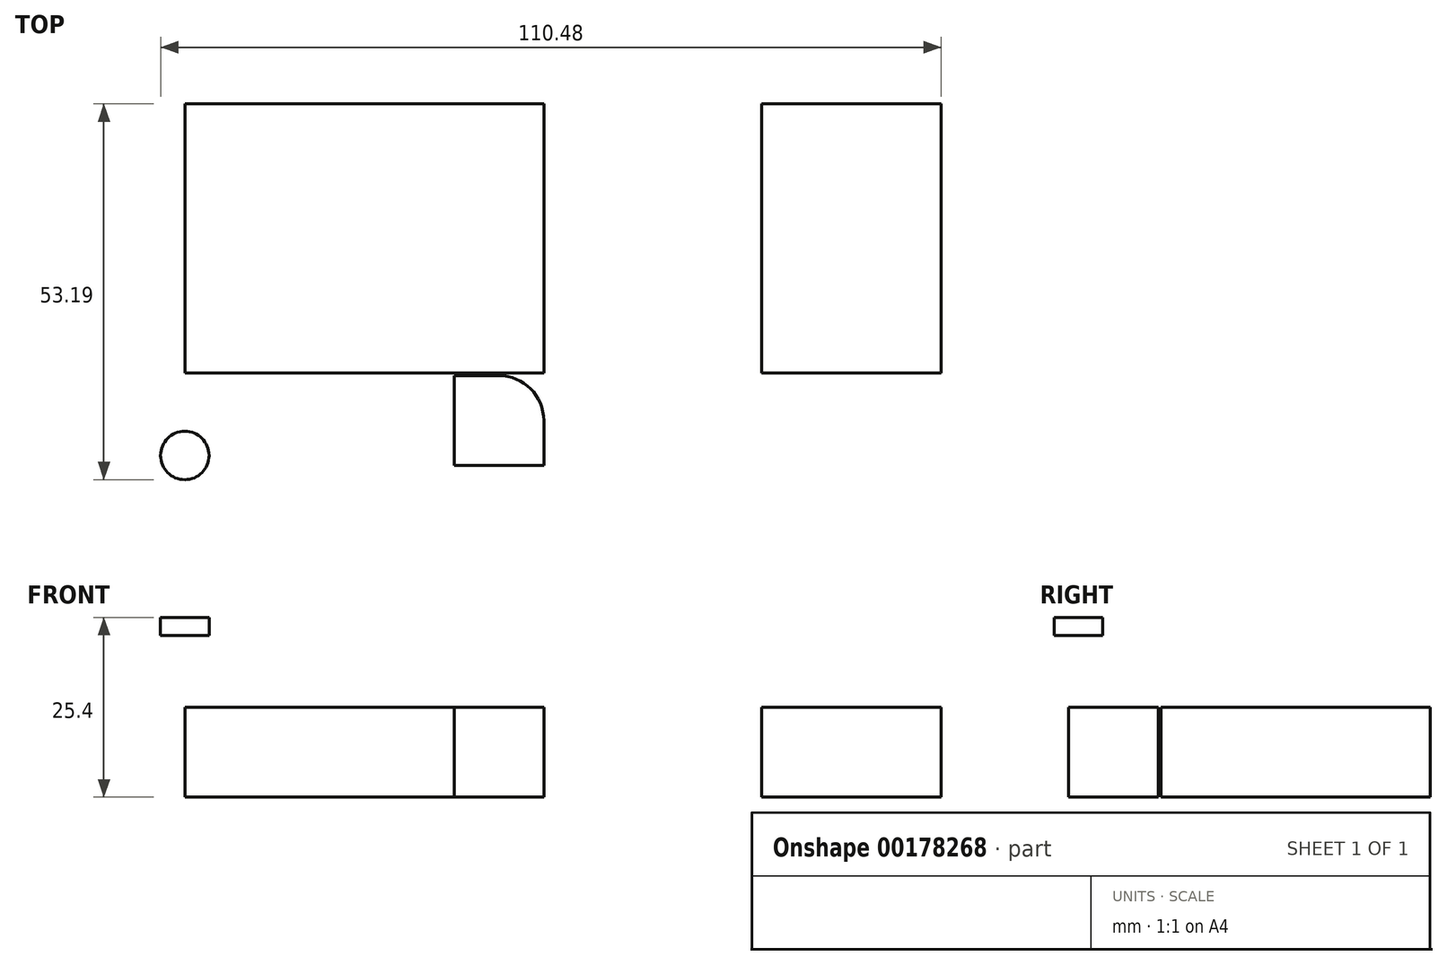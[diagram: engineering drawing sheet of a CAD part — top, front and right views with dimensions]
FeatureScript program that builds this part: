
annotation { "Feature Type Name" : "Feature", "Feature Type Description" : "" }
export const myFeature = defineFeature(function(context is Context, id is Id, definition is map)
    precondition{}
    {
        {
            var Q0;
            Q0=qCreatedBy(makeId("Top.planeOp"),FACE);
            var sketch = newSketch(context, id + "F0", { "sketchPlane" : qUnion([Q0])});
            skLineSegment(sketch, "E0.bottom", {"start": v(0, 0) * mm, "end": v(107.05, 0) * mm});
            skLineSegment(sketch, "E0.top", {"start": v(0, 66.76) * mm, "end": v(107.05, 66.76) * mm});
            skLineSegment(sketch, "E0.left", {"start": v(0, 0) * mm, "end": v(0, 66.76) * mm});
            skLineSegment(sketch, "E0.right", {"start": v(107.05, 0) * mm, "end": v(107.05, 66.76) * mm});
            skSolve(sketch);
        }
        {
            var Q0;
            Q0=qCreatedBy(makeId("Top.planeOp"),FACE);
            var sketch = newSketch(context, id + "F1", { "sketchPlane" : qUnion([Q0])});
            skLineSegment(sketch, "E1.bottom", {"start": v(0, 28.66) * mm, "end": v(50.8, 28.66) * mm});
            skLineSegment(sketch, "E1.top", {"start": v(0, 66.76) * mm, "end": v(50.8, 66.76) * mm});
            skLineSegment(sketch, "E1.left", {"start": v(0, 28.66) * mm, "end": v(0, 66.76) * mm});
            skLineSegment(sketch, "E1.right", {"start": v(50.8, 28.66) * mm, "end": v(50.8, 66.76) * mm});
            skLineSegment(sketch, "E2.bottom", {"start": v(81.65, 66.76) * mm, "end": v(107.05, 66.76) * mm});
            skLineSegment(sketch, "E2.top", {"start": v(81.65, 28.66) * mm, "end": v(107.05, 28.66) * mm});
            skLineSegment(sketch, "E2.left", {"start": v(81.65, 66.76) * mm, "end": v(81.65, 28.66) * mm});
            skLineSegment(sketch, "E2.right", {"start": v(107.05, 66.76) * mm, "end": v(107.05, 28.66) * mm});
            skLineSegment(sketch, "E3.bottom", {"start": v(38.1, 28.3) * mm, "end": v(44.45, 28.3) * mm});
            skLineSegment(sketch, "E3.top", {"start": v(38.1, 15.6) * mm, "end": v(50.8, 15.6) * mm});
            skLineSegment(sketch, "E3.left", {"start": v(38.1, 28.3) * mm, "end": v(38.1, 15.6) * mm});
            skLineSegment(sketch, "E3.right", {"start": v(50.8, 21.95) * mm, "end": v(50.8, 15.6) * mm});
            skPoint(sketch, "E4.visualSharp", {"position": v(50.8, 28.3) * mm});
            skArc(sketch, "E4.filletArc", {"start": v(50.8, 21.95) * mm, "mid": v(48.94, 26.44) * mm, "end": v(44.45, 28.3) * mm});
            skSolve(sketch);
        }
        {
            var Q0;
            Q0=qCreatedBy(makeId("Front.planeOp"),FACE);
            var sketch = newSketch(context, id + "F2", { "sketchPlane" : qUnion([Q0])});
            skLineSegment(sketch, "E5", {"start": v(0, 24.31) * mm, "end": v(6.35, 24.31) * mm});
            skLineSegment(sketch, "E6", {"start": v(6.35, 24.31) * mm, "end": v(24.31, 6.35) * mm});
            skLineSegment(sketch, "E7", {"start": v(24.31, 6.35) * mm, "end": v(24.31, 0) * mm});
            skLineSegment(sketch, "E8", {"start": v(0, 40.3) * mm, "end": v(0, 0) * mm, "construction": true});
            skSolve(sketch);
        }
        {
            var Q0;
            Q0=sQuery(id+"F2.wireOp",EDGE,"E6");
            var Q1;
            Q1=sQuery(id+"F2.wireOp",EDGE,"E7");
            var Q2;
            Q2=sQuery(id+"F2.wireOp",EDGE,"E5");
            var Q3;
            Q3=sQuery(id+"F2.wireOp",EDGE,"E8");
            revolve(context, id + "F3", {"bodyType" : ToolBodyType.SURFACE, "surfaceEntities" : qUnion([Q0, Q1, Q2]), "axis" : qUnion([Q3]), "revolveType" : RevolveType.FULL});
        }
        {
            var Q0;
            Q0=qCreatedBy(makeId("Top.planeOp"),FACE);
            cPlane(context, id + "F4", {"entities" : qUnion([Q0]), "cplaneType" : CPlaneType.OFFSET, "offset" : 25.4 * mm, "width" : 152.4 * mm, "height" : 152.4 * mm});
        }
        {
            var Q0;
            Q0=qCreatedBy(id+"F4.planeOp",FACE);
            var sketch = newSketch(context, id + "F5", { "sketchPlane" : qUnion([Q0])});
            skCircle(sketch, "E9", {"center": v(0, 17) * mm, "radius": 3.43 * mm});
            skSolve(sketch);
        }
        {
            var Q0;
            Q0=makeQuery(id+"F5.imprint","IMPRINT",FACE,{"disambiguationData":[TD([[makeQuery(id+"F5.imprint","IMPRINT",EDGE,{"derivedFrom":sQuery(id+"F5.wireOp",EDGE,"E9")}),1.0]])]});
            var Q1;
            Q1=sQuery(id+"F5.wireOp",EDGE,"E9");
            extrude(context, id + "F6", {"entities" : qUnion([Q0]), "surfaceEntities" : qUnion([Q1]), "oppositeDirection" : true, "depth" : 2.54 * mm});
        }
        {
            var Q0;
            Q0 = qSketchRegion(id + "F1", true);
            extrude(context, id + "F7", {"entities" : qUnion([Q0]), "depth" : 12.7 * mm});
        }
    });
